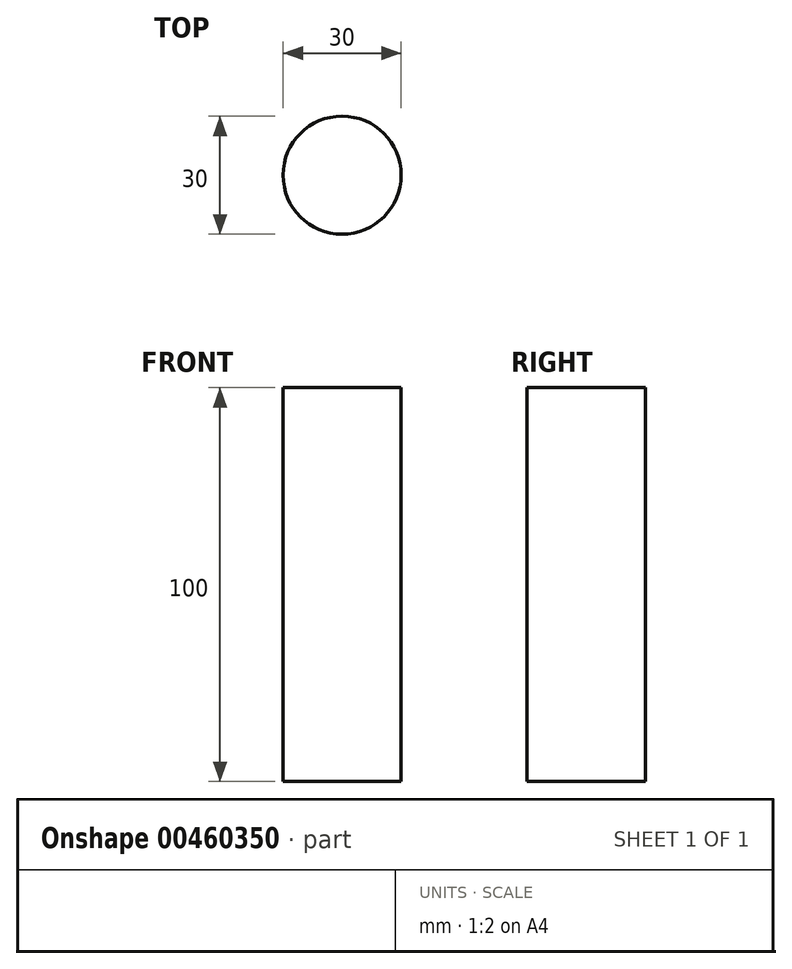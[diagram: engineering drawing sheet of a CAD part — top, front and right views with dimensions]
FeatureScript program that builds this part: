
annotation { "Feature Type Name" : "Feature", "Feature Type Description" : "" }
export const myFeature = defineFeature(function(context is Context, id is Id, definition is map)
    precondition{}
    {
        {
            var Q0;
            Q0=qCreatedBy(makeId("Top.planeOp"),FACE);
            var sketch = newSketch(context, id + "F0", { "sketchPlane" : qUnion([Q0])});
            skCircle(sketch, "E0", {"center": v(0, 0) * mm, "radius": 15 * mm});
            skSolve(sketch);
        }
        {
            var Q0;
            Q0=makeQuery(id+"F0.imprint","IMPRINT",FACE,{"disambiguationData":[TD([[makeQuery(id+"F0.imprint","IMPRINT",EDGE,{"derivedFrom":sQuery(id+"F0.wireOp",EDGE,"E0")}),1.0]])]});
            var Q1;
            Q1=sQuery(id+"F0.wireOp",EDGE,"E0");
            extrude(context, id + "F1", {"entities" : qUnion([Q0]), "surfaceEntities" : qUnion([Q1]), "depth" : 100 * mm});
        }
    });
